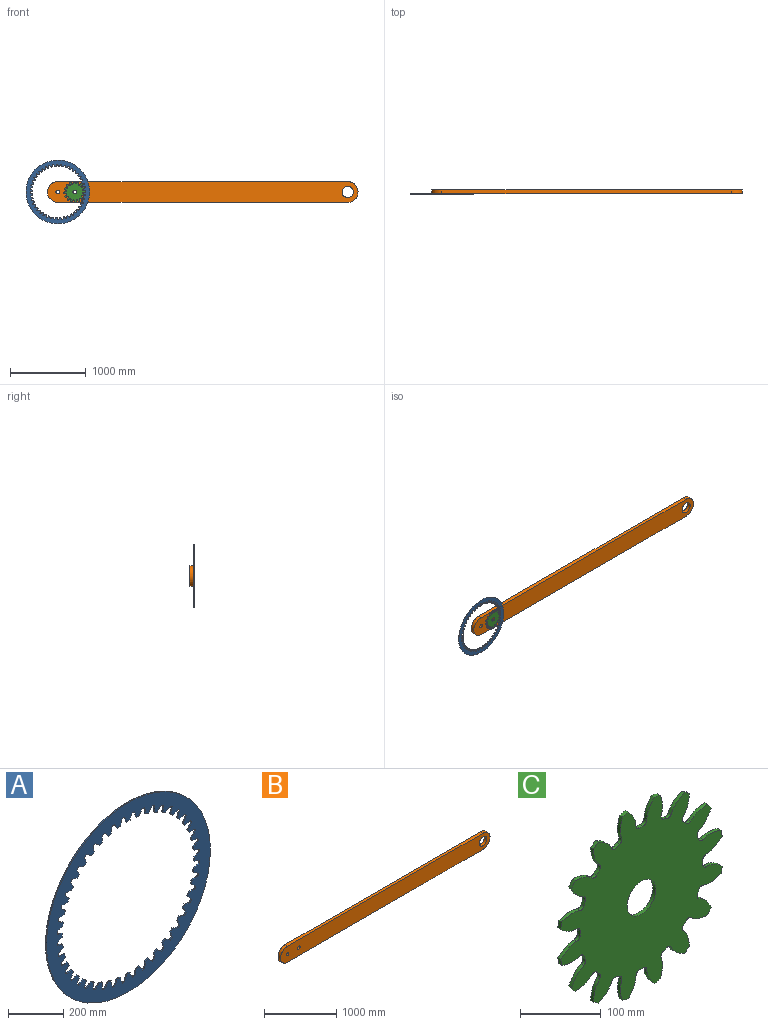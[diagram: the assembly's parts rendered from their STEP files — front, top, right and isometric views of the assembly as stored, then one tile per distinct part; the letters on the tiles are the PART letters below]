
ASSEMBLY  parts=3 mates=2
PART A: 179 faces, bbox 840x5x840 mm
  f0: cylinder r=419.99mm len=839.98mm, axis (0,1,0), area 13194.4mm2, adj f1,f2
  f1: plane 839.98x839.98mm, normal (0,-1,0), area 166526.1mm2, adj f0,f3,f4,f5,f6,f7,f8,f9
  f2: plane 839.98x839.98mm, normal (0,1,0), area 166526.1mm2, adj f0,f3,f4,f5,f6,f7,f8,f9
  f3: cylinder r=365.9mm len=11.89mm, axis (0,1,0), area 60.8mm2, adj f1,f2,f173,f178
  f4: cylinder r=365.9mm len=11.4mm, axis (0,1,0), area 60.8mm2, adj f1,f2,f170,f175
  f5: cylinder r=365.9mm len=10.68mm, axis (0,1,0), area 60.8mm2, adj f1,f2,f167,f172
  f6: cylinder r=365.9mm len=9.74mm, axis (0,1,0), area 60.8mm2, adj f1,f2,f161,f169
  f7: cylinder r=365.9mm len=9.74mm, axis (0,1,0), area 60.8mm2, adj f1,f2,f158,f166
  f8: cylinder r=365.9mm len=8.6mm, axis (0,1,0), area 60.8mm2, adj f1,f2,f163,f164
  f9: cylinder r=365.9mm len=10.68mm, axis (0,1,0), area 60.8mm2, adj f1,f2,f155,f160
  f10: cylinder r=365.9mm len=11.4mm, axis (0,1,0), area 60.8mm2, adj f1,f2,f152,f157
  f11: cylinder r=365.9mm len=11.89mm, axis (0,1,0), area 60.8mm2, adj f1,f2,f149,f154
  f12: cylinder r=365.9mm len=12.14mm, axis (0,1,0), area 60.8mm2, adj f1,f2,f146,f151
  f13: cylinder r=365.9mm len=12.14mm, axis (0,1,0), area 60.8mm2, adj f1,f2,f143,f148
  f14: cylinder r=365.9mm len=11.89mm, axis (0,1,0), area 60.8mm2, adj f1,f2,f140,f145
  f15: cylinder r=365.9mm len=11.4mm, axis (0,1,0), area 60.8mm2, adj f1,f2,f137,f142
  f16: cylinder r=365.9mm len=10.68mm, axis (0,1,0), area 60.8mm2, adj f1,f2,f134,f139
  f17: cylinder r=365.9mm len=9.74mm, axis (0,1,0), area 60.8mm2, adj f1,f2,f131,f136
  f18: cylinder r=365.9mm len=8.6mm, axis (0,1,0), area 60.8mm2, adj f1,f2,f128,f133
  f19: cylinder r=365.9mm len=9.74mm, axis (0,1,0), area 60.8mm2, adj f1,f2,f125,f130
  f20: cylinder r=365.9mm len=10.68mm, axis (0,1,0), area 60.8mm2, adj f1,f2,f122,f127
  f21: cylinder r=365.9mm len=11.4mm, axis (0,1,0), area 60.8mm2, adj f1,f2,f119,f124
  f22: cylinder r=365.9mm len=11.89mm, axis (0,1,0), area 60.8mm2, adj f1,f2,f116,f121
  f23: cylinder r=365.9mm len=12.14mm, axis (0,1,0), area 60.8mm2, adj f1,f2,f113,f118
  f24: cylinder r=365.9mm len=12.14mm, axis (0,1,0), area 60.8mm2, adj f1,f2,f110,f115
  f25: cylinder r=365.9mm len=11.89mm, axis (0,1,0), area 60.8mm2, adj f1,f2,f107,f112
  f26: cylinder r=365.9mm len=11.4mm, axis (0,1,0), area 60.8mm2, adj f1,f2,f104,f109
  f27: cylinder r=365.9mm len=10.68mm, axis (0,1,0), area 60.8mm2, adj f1,f2,f101,f106
  f28: cylinder r=365.9mm len=9.74mm, axis (0,1,0), area 60.8mm2, adj f1,f2,f95,f103
  f29: cylinder r=365.9mm len=9.74mm, axis (0,1,0), area 60.8mm2, adj f1,f2,f92,f100
  f30: cylinder r=365.9mm len=8.6mm, axis (0,1,0), area 60.8mm2, adj f1,f2,f97,f98
  f31: cylinder r=365.9mm len=10.68mm, axis (0,1,0), area 60.8mm2, adj f1,f2,f89,f94
  f32: cylinder r=365.9mm len=11.4mm, axis (0,1,0), area 60.8mm2, adj f1,f2,f86,f91
  f33: cylinder r=365.9mm len=11.89mm, axis (0,1,0), area 60.8mm2, adj f1,f2,f83,f88
  f34: cylinder r=365.9mm len=12.14mm, axis (0,1,0), area 60.8mm2, adj f1,f2,f47,f85
  f35: cylinder r=365.9mm len=12.14mm, axis (0,1,0), area 60.8mm2, adj f1,f2,f82,f176
  f36: cylinder r=365.9mm len=12.14mm, axis (0,1,0), area 60.8mm2, adj f1,f2,f79,f80
  f37: cylinder r=365.9mm len=11.89mm, axis (0,1,0), area 60.8mm2, adj f1,f2,f76,f77
  f38: cylinder r=365.9mm len=11.4mm, axis (0,1,0), area 60.8mm2, adj f1,f2,f73,f74
  f39: cylinder r=365.9mm len=9.74mm, axis (0,1,0), area 60.8mm2, adj f1,f2,f65,f70
  f40: cylinder r=365.9mm len=8.6mm, axis (0,1,0), area 60.8mm2, adj f1,f2,f62,f67
  f41: cylinder r=365.9mm len=9.74mm, axis (0,1,0), area 60.8mm2, adj f1,f2,f59,f64
  f42: cylinder r=365.9mm len=10.68mm, axis (0,1,0), area 60.8mm2, adj f1,f2,f61,f71
  f43: cylinder r=365.9mm len=10.68mm, axis (0,1,0), area 60.8mm2, adj f1,f2,f58,f68
  f44: cylinder r=365.9mm len=11.4mm, axis (0,1,0), area 60.8mm2, adj f1,f2,f55,f56
  f45: cylinder r=365.9mm len=11.89mm, axis (0,1,0), area 60.8mm2, adj f1,f2,f52,f53
  f46: cylinder r=365.9mm len=12.14mm, axis (0,1,0), area 60.8mm2, adj f1,f2,f49,f50
  f47: extruded ~26.87x11.39mm, area 146.3mm2, adj f1,f2,f34,f48
  f48: cylinder r=338.59mm len=17.28mm, axis (0,1,0), area 86.4mm2, adj f1,f2,f47,f49
  f49: extruded ~26.87x11.39mm, area 146.3mm2, adj f1,f2,f46,f48
  f50: extruded ~28.22x7.45mm, area 146.3mm2, adj f1,f2,f46,f51
  f51: cylinder r=338.59mm len=17.1mm, axis (0,1,0), area 86.4mm2, adj f1,f2,f50,f52
  f52: extruded ~24.98x15.1mm, area 146.3mm2, adj f1,f2,f45,f51
  f53: extruded ~28.99x5mm, area 146.3mm2, adj f1,f2,f45,f54
  f54: cylinder r=338.59mm len=16.58mm, axis (0,1,0), area 86.4mm2, adj f1,f2,f53,f55
  f55: extruded ~22.57x18.5mm, area 146.3mm2, adj f1,f2,f44,f54
  f56: extruded ~29.18x5mm, area 146.3mm2, adj f1,f2,f44,f57
  f57: cylinder r=338.59mm len=15.71mm, axis (0,1,0), area 86.4mm2, adj f1,f2,f56,f58
  f58: extruded ~21.53x19.71mm, area 146.3mm2, adj f1,f2,f43,f57
  f59: extruded ~24.11x16.45mm, area 146.3mm2, adj f1,f2,f41,f60
  f60: cylinder r=338.59mm len=14.53mm, axis (0,1,0), area 86.4mm2, adj f1,f2,f59,f61
  f61: extruded ~28.77x5mm, area 146.3mm2, adj f1,f2,f42,f60
  f62: extruded ~26.21x12.85mm, area 146.3mm2, adj f1,f2,f40,f63
  f63: cylinder r=338.59mm len=13.06mm, axis (0,1,0), area 86.4mm2, adj f1,f2,f62,f64
  f64: extruded ~27.77x8.99mm, area 146.3mm2, adj f1,f2,f41,f63
  f65: extruded ~27.77x8.99mm, area 146.3mm2, adj f1,f2,f39,f66
  f66: cylinder r=338.59mm len=13.06mm, axis (0,1,0), area 86.4mm2, adj f1,f2,f65,f67
  f67: extruded ~26.21x12.85mm, area 146.3mm2, adj f1,f2,f40,f66
  f68: extruded ~28.77x5mm, area 146.3mm2, adj f1,f2,f43,f69
  f69: cylinder r=338.59mm len=14.53mm, axis (0,1,0), area 86.4mm2, adj f1,f2,f68,f70
  f70: extruded ~24.11x16.45mm, area 146.3mm2, adj f1,f2,f39,f69
  f71: extruded ~21.53x19.71mm, area 146.3mm2, adj f1,f2,f42,f72
  f72: cylinder r=338.59mm len=15.71mm, axis (0,1,0), area 86.4mm2, adj f1,f2,f71,f73
  f73: extruded ~29.18x5mm, area 146.3mm2, adj f1,f2,f38,f72
  f74: extruded ~22.57x18.5mm, area 146.3mm2, adj f1,f2,f38,f75
  f75: cylinder r=338.59mm len=16.58mm, axis (0,1,0), area 86.4mm2, adj f1,f2,f74,f76
  f76: extruded ~28.99x5mm, area 146.3mm2, adj f1,f2,f37,f75
  f77: extruded ~24.98x15.1mm, area 146.3mm2, adj f1,f2,f37,f78
  f78: cylinder r=338.59mm len=17.1mm, axis (0,1,0), area 86.4mm2, adj f1,f2,f77,f79
  f79: extruded ~28.22x7.45mm, area 146.3mm2, adj f1,f2,f36,f78
  f80: extruded ~26.87x11.39mm, area 146.3mm2, adj f1,f2,f36,f81
  f81: cylinder r=338.59mm len=17.28mm, axis (0,1,0), area 86.4mm2, adj f1,f2,f80,f82
  f82: extruded ~26.87x11.39mm, area 146.3mm2, adj f1,f2,f35,f81
  f83: extruded ~24.98x15.1mm, area 146.3mm2, adj f1,f2,f33,f84
  f84: cylinder r=338.59mm len=17.1mm, axis (0,1,0), area 86.4mm2, adj f1,f2,f83,f85
  f85: extruded ~28.22x7.45mm, area 146.3mm2, adj f1,f2,f34,f84
  f86: extruded ~22.57x18.5mm, area 146.3mm2, adj f1,f2,f32,f87
  f87: cylinder r=338.59mm len=16.58mm, axis (0,1,0), area 86.4mm2, adj f1,f2,f86,f88
  f88: extruded ~28.99x5mm, area 146.3mm2, adj f1,f2,f33,f87
  f89: extruded ~21.53x19.71mm, area 146.3mm2, adj f1,f2,f31,f90
  f90: cylinder r=338.59mm len=15.71mm, axis (0,1,0), area 86.4mm2, adj f1,f2,f89,f91
  f91: extruded ~29.18x5mm, area 146.3mm2, adj f1,f2,f32,f90
  f92: extruded ~24.11x16.45mm, area 146.3mm2, adj f1,f2,f29,f93
  f93: cylinder r=338.59mm len=14.53mm, axis (0,1,0), area 86.4mm2, adj f1,f2,f92,f94
  f94: extruded ~28.77x5mm, area 146.3mm2, adj f1,f2,f31,f93
  f95: extruded ~27.77x8.99mm, area 146.3mm2, adj f1,f2,f28,f96
  f96: cylinder r=338.59mm len=13.06mm, axis (0,1,0), area 86.4mm2, adj f1,f2,f95,f97
  f97: extruded ~26.21x12.85mm, area 146.3mm2, adj f1,f2,f30,f96
  f98: extruded ~26.21x12.85mm, area 146.3mm2, adj f1,f2,f30,f99
  f99: cylinder r=338.59mm len=13.06mm, axis (0,1,0), area 86.4mm2, adj f1,f2,f98,f100
  f100: extruded ~27.77x8.99mm, area 146.3mm2, adj f1,f2,f29,f99
  f101: extruded ~28.77x5mm, area 146.3mm2, adj f1,f2,f27,f102
  f102: cylinder r=338.59mm len=14.53mm, axis (0,1,0), area 86.4mm2, adj f1,f2,f101,f103
  f103: extruded ~24.11x16.45mm, area 146.3mm2, adj f1,f2,f28,f102
  f104: extruded ~29.18x5mm, area 146.3mm2, adj f1,f2,f26,f105
  f105: cylinder r=338.59mm len=15.71mm, axis (0,1,0), area 86.4mm2, adj f1,f2,f104,f106
  f106: extruded ~21.53x19.71mm, area 146.3mm2, adj f1,f2,f27,f105
  f107: extruded ~28.99x5mm, area 146.3mm2, adj f1,f2,f25,f108
  f108: cylinder r=338.59mm len=16.58mm, axis (0,1,0), area 86.4mm2, adj f1,f2,f107,f109
  f109: extruded ~22.57x18.5mm, area 146.3mm2, adj f1,f2,f26,f108
  f110: extruded ~28.22x7.45mm, area 146.3mm2, adj f1,f2,f24,f111
  f111: cylinder r=338.59mm len=17.1mm, axis (0,1,0), area 86.4mm2, adj f1,f2,f110,f112
  f112: extruded ~24.98x15.1mm, area 146.3mm2, adj f1,f2,f25,f111
  f113: extruded ~26.87x11.39mm, area 146.3mm2, adj f1,f2,f23,f114
  f114: cylinder r=338.59mm len=17.28mm, axis (0,1,0), area 86.4mm2, adj f1,f2,f113,f115
  f115: extruded ~26.87x11.39mm, area 146.3mm2, adj f1,f2,f24,f114
  f116: extruded ~24.98x15.1mm, area 146.3mm2, adj f1,f2,f22,f117
  f117: cylinder r=338.59mm len=17.1mm, axis (0,1,0), area 86.4mm2, adj f1,f2,f116,f118
  f118: extruded ~28.22x7.45mm, area 146.3mm2, adj f1,f2,f23,f117
  f119: extruded ~22.57x18.5mm, area 146.3mm2, adj f1,f2,f21,f120
  f120: cylinder r=338.59mm len=16.58mm, axis (0,1,0), area 86.4mm2, adj f1,f2,f119,f121
  f121: extruded ~28.99x5mm, area 146.3mm2, adj f1,f2,f22,f120
  f122: extruded ~21.53x19.71mm, area 146.3mm2, adj f1,f2,f20,f123
  f123: cylinder r=338.59mm len=15.71mm, axis (0,1,0), area 86.4mm2, adj f1,f2,f122,f124
  f124: extruded ~29.18x5mm, area 146.3mm2, adj f1,f2,f21,f123
  f125: extruded ~24.11x16.45mm, area 146.3mm2, adj f1,f2,f19,f126
  f126: cylinder r=338.59mm len=14.53mm, axis (0,1,0), area 86.4mm2, adj f1,f2,f125,f127
  f127: extruded ~28.77x5mm, area 146.3mm2, adj f1,f2,f20,f126
  f128: extruded ~26.21x12.85mm, area 146.3mm2, adj f1,f2,f18,f129
  f129: cylinder r=338.59mm len=13.06mm, axis (0,1,0), area 86.4mm2, adj f1,f2,f128,f130
  f130: extruded ~27.77x8.99mm, area 146.3mm2, adj f1,f2,f19,f129
  f131: extruded ~27.77x8.99mm, area 146.3mm2, adj f1,f2,f17,f132
  f132: cylinder r=338.59mm len=13.06mm, axis (0,1,0), area 86.4mm2, adj f1,f2,f131,f133
  f133: extruded ~26.21x12.85mm, area 146.3mm2, adj f1,f2,f18,f132
  f134: extruded ~28.77x5mm, area 146.3mm2, adj f1,f2,f16,f135
  f135: cylinder r=338.59mm len=14.53mm, axis (0,1,0), area 86.4mm2, adj f1,f2,f134,f136
  f136: extruded ~24.11x16.45mm, area 146.3mm2, adj f1,f2,f17,f135
  f137: extruded ~29.18x5mm, area 146.3mm2, adj f1,f2,f15,f138
  f138: cylinder r=338.59mm len=15.71mm, axis (0,1,0), area 86.4mm2, adj f1,f2,f137,f139
  f139: extruded ~21.53x19.71mm, area 146.3mm2, adj f1,f2,f16,f138
  f140: extruded ~28.99x5mm, area 146.3mm2, adj f1,f2,f14,f141
  f141: cylinder r=338.59mm len=16.58mm, axis (0,1,0), area 86.4mm2, adj f1,f2,f140,f142
  f142: extruded ~22.57x18.5mm, area 146.3mm2, adj f1,f2,f15,f141
  f143: extruded ~28.22x7.45mm, area 146.3mm2, adj f1,f2,f13,f144
  f144: cylinder r=338.59mm len=17.1mm, axis (0,1,0), area 86.4mm2, adj f1,f2,f143,f145
  f145: extruded ~24.98x15.1mm, area 146.3mm2, adj f1,f2,f14,f144
  f146: extruded ~26.87x11.39mm, area 146.3mm2, adj f1,f2,f12,f147
  f147: cylinder r=338.59mm len=17.28mm, axis (0,1,0), area 86.4mm2, adj f1,f2,f146,f148
  f148: extruded ~26.87x11.39mm, area 146.3mm2, adj f1,f2,f13,f147
  f149: extruded ~24.98x15.1mm, area 146.3mm2, adj f1,f2,f11,f150
  f150: cylinder r=338.59mm len=17.1mm, axis (0,1,0), area 86.4mm2, adj f1,f2,f149,f151
  f151: extruded ~28.22x7.45mm, area 146.3mm2, adj f1,f2,f12,f150
  f152: extruded ~22.57x18.5mm, area 146.3mm2, adj f1,f2,f10,f153
  f153: cylinder r=338.59mm len=16.58mm, axis (0,1,0), area 86.4mm2, adj f1,f2,f152,f154
  f154: extruded ~28.99x5mm, area 146.3mm2, adj f1,f2,f11,f153
  f155: extruded ~21.53x19.71mm, area 146.3mm2, adj f1,f2,f9,f156
  f156: cylinder r=338.59mm len=15.71mm, axis (0,1,0), area 86.4mm2, adj f1,f2,f155,f157
  f157: extruded ~29.18x5mm, area 146.3mm2, adj f1,f2,f10,f156
  f158: extruded ~24.11x16.45mm, area 146.3mm2, adj f1,f2,f7,f159
  f159: cylinder r=338.59mm len=14.53mm, axis (0,1,0), area 86.4mm2, adj f1,f2,f158,f160
  f160: extruded ~28.77x5mm, area 146.3mm2, adj f1,f2,f9,f159
  f161: extruded ~27.77x8.99mm, area 146.3mm2, adj f1,f2,f6,f162
  f162: cylinder r=338.59mm len=13.06mm, axis (0,1,0), area 86.4mm2, adj f1,f2,f161,f163
  f163: extruded ~26.21x12.85mm, area 146.3mm2, adj f1,f2,f8,f162
  f164: extruded ~26.21x12.85mm, area 146.3mm2, adj f1,f2,f8,f165
  f165: cylinder r=338.59mm len=13.06mm, axis (0,1,0), area 86.4mm2, adj f1,f2,f164,f166
  f166: extruded ~27.77x8.99mm, area 146.3mm2, adj f1,f2,f7,f165
  f167: extruded ~28.77x5mm, area 146.3mm2, adj f1,f2,f5,f168
  f168: cylinder r=338.59mm len=14.53mm, axis (0,1,0), area 86.4mm2, adj f1,f2,f167,f169
  f169: extruded ~24.11x16.45mm, area 146.3mm2, adj f1,f2,f6,f168
  f170: extruded ~29.18x5mm, area 146.3mm2, adj f1,f2,f4,f171
  f171: cylinder r=338.59mm len=15.71mm, axis (0,1,0), area 86.4mm2, adj f1,f2,f170,f172
  f172: extruded ~21.53x19.71mm, area 146.3mm2, adj f1,f2,f5,f171
  f173: extruded ~28.99x5mm, area 146.3mm2, adj f1,f2,f3,f174
  f174: cylinder r=338.59mm len=16.58mm, axis (0,1,0), area 86.4mm2, adj f1,f2,f173,f175
  f175: extruded ~22.57x18.5mm, area 146.3mm2, adj f1,f2,f4,f174
  f176: extruded ~28.22x7.45mm, area 146.3mm2, adj f1,f2,f35,f177
  f177: cylinder r=338.59mm len=17.1mm, axis (0,1,0), area 86.4mm2, adj f1,f2,f176,f178
  f178: extruded ~24.98x15.1mm, area 146.3mm2, adj f1,f2,f3,f177
PART B: 9 faces, bbox 4181.6x50x272 mm
  f0: plane 3828x50mm, normal (0,0,-1), area 191400mm2, adj f1,f6,f7,f8
  f1: extruded ~272x136mm, area 21362.8mm2, adj f0,f2,f7,f8
  f2: plane 3828x50mm, normal (0,0,1), area 191400mm2, adj f1,f6,f7,f8
  f3: cylinder r=75mm len=150mm, axis (0,1,0), area 23561.9mm2, adj f7,f8
  f4: cylinder r=25mm len=50mm, axis (0,1,0), area 7854mm2, adj f7,f8
  f5: cylinder r=25mm len=50mm, axis (0,1,0), area 7854mm2, adj f7,f8
  f6: extruded ~272x136mm, area 21362.8mm2, adj f0,f2,f7,f8
  f7: plane 4181.6x272mm, normal (0,-1,0), area 1077690.6mm2, adj f0,f1,f2,f3,f4,f5,f6
  f8: plane 4181.6x272mm, normal (0,1,0), area 1077690.6mm2, adj f0,f1,f2,f3,f4,f5,f6
PART C: 99 faces, bbox 283.1x5x283.1 mm
  f0: extruded ~28.56x13.33mm, area 161.7mm2, adj f64,f65,f66,f67
  f1: cylinder r=107.37mm len=6.56mm, axis (0,1,0), area 32.8mm2, adj f65,f66,f67,f68
  f2: extruded ~28.56x13.33mm, area 161.7mm2, adj f3,f65,f66,f68
  f3: cylinder r=143.16mm len=10.38mm, axis (0,1,0), area 52.9mm2, adj f2,f4,f65,f66
  f4: extruded ~31.48x5mm, area 161.7mm2, adj f3,f65,f66,f69
  f5: cylinder r=107.37mm len=6.06mm, axis (0,1,0), area 32.8mm2, adj f65,f66,f69,f70
  f6: extruded ~23.24x21.28mm, area 161.7mm2, adj f7,f65,f66,f70
  f7: cylinder r=143.16mm len=8.8mm, axis (0,1,0), area 52.9mm2, adj f6,f8,f65,f66
  f8: extruded ~29.62x10.77mm, area 161.7mm2, adj f7,f65,f66,f71
  f9: cylinder r=107.37mm len=5mm, axis (0,1,0), area 32.8mm2, adj f65,f66,f71,f72
  f10: extruded ~29.62x10.77mm, area 161.7mm2, adj f11,f65,f66,f72
  f11: cylinder r=143.16mm len=8.8mm, axis (0,1,0), area 52.9mm2, adj f10,f12,f65,f66
  f12: extruded ~23.24x21.28mm, area 161.7mm2, adj f11,f65,f66,f73
  f13: cylinder r=107.37mm len=6.06mm, axis (0,1,0), area 32.8mm2, adj f65,f66,f73,f74
  f14: extruded ~31.48x5mm, area 161.7mm2, adj f15,f65,f66,f74
  f15: cylinder r=143.16mm len=10.38mm, axis (0,1,0), area 52.9mm2, adj f14,f16,f65,f66
  f16: extruded ~28.56x13.33mm, area 161.7mm2, adj f15,f65,f66,f75
  f17: cylinder r=107.37mm len=6.56mm, axis (0,1,0), area 32.8mm2, adj f65,f66,f75,f76
  f18: extruded ~28.56x13.33mm, area 161.7mm2, adj f19,f65,f66,f76
  f19: cylinder r=143.16mm len=10.38mm, axis (0,1,0), area 52.9mm2, adj f18,f20,f65,f66
  f20: extruded ~31.48x5mm, area 161.7mm2, adj f19,f65,f66,f77
  f21: cylinder r=107.37mm len=6.06mm, axis (0,1,0), area 32.8mm2, adj f65,f66,f77,f78
  f22: extruded ~23.24x21.28mm, area 161.7mm2, adj f23,f65,f66,f78
  f23: cylinder r=143.16mm len=8.8mm, axis (0,1,0), area 52.9mm2, adj f22,f24,f65,f66
  f24: extruded ~29.62x10.77mm, area 161.7mm2, adj f23,f65,f66,f79
  f25: cylinder r=107.37mm len=5mm, axis (0,1,0), area 32.8mm2, adj f65,f66,f79,f80
  f26: extruded ~29.62x10.77mm, area 161.7mm2, adj f27,f65,f66,f80
  f27: cylinder r=143.16mm len=8.8mm, axis (0,1,0), area 52.9mm2, adj f26,f28,f65,f66
  f28: extruded ~23.24x21.28mm, area 161.7mm2, adj f27,f65,f66,f81
  f29: cylinder r=107.37mm len=6.06mm, axis (0,1,0), area 32.8mm2, adj f65,f66,f81,f82
  f30: extruded ~31.48x5mm, area 161.7mm2, adj f31,f65,f66,f82
  f31: cylinder r=143.16mm len=10.38mm, axis (0,1,0), area 52.9mm2, adj f30,f32,f65,f66
  f32: extruded ~28.56x13.33mm, area 161.7mm2, adj f31,f65,f66,f83
  f33: cylinder r=107.37mm len=6.56mm, axis (0,1,0), area 32.8mm2, adj f65,f66,f83,f84
  f34: extruded ~28.56x13.33mm, area 161.7mm2, adj f35,f65,f66,f84
  f35: cylinder r=143.16mm len=10.38mm, axis (0,1,0), area 52.9mm2, adj f34,f36,f65,f66
  f36: extruded ~31.48x5mm, area 161.7mm2, adj f35,f65,f66,f85
  f37: cylinder r=107.37mm len=6.06mm, axis (0,1,0), area 32.8mm2, adj f65,f66,f85,f86
  f38: extruded ~23.24x21.28mm, area 161.7mm2, adj f39,f65,f66,f86
  f39: cylinder r=143.16mm len=8.8mm, axis (0,1,0), area 52.9mm2, adj f38,f40,f65,f66
  f40: extruded ~29.62x10.77mm, area 161.7mm2, adj f39,f65,f66,f87
  f41: cylinder r=107.37mm len=5mm, axis (0,1,0), area 32.8mm2, adj f65,f66,f87,f88
  f42: extruded ~29.62x10.77mm, area 161.7mm2, adj f43,f65,f66,f88
  f43: cylinder r=143.16mm len=8.8mm, axis (0,1,0), area 52.9mm2, adj f42,f44,f65,f66
  f44: extruded ~23.24x21.28mm, area 161.7mm2, adj f43,f65,f66,f89
  f45: cylinder r=107.37mm len=6.06mm, axis (0,1,0), area 32.8mm2, adj f65,f66,f89,f90
  f46: extruded ~31.48x5mm, area 161.7mm2, adj f47,f65,f66,f90
  f47: cylinder r=143.16mm len=10.38mm, axis (0,1,0), area 52.9mm2, adj f46,f48,f65,f66
  f48: extruded ~28.56x13.33mm, area 161.7mm2, adj f47,f65,f66,f91
  f49: cylinder r=107.37mm len=6.56mm, axis (0,1,0), area 32.8mm2, adj f65,f66,f91,f92
  f50: extruded ~28.56x13.33mm, area 161.7mm2, adj f51,f65,f66,f92
  f51: cylinder r=143.16mm len=10.38mm, axis (0,1,0), area 52.9mm2, adj f50,f52,f65,f66
  f52: extruded ~31.48x5mm, area 161.7mm2, adj f51,f65,f66,f93
  f53: cylinder r=107.37mm len=6.06mm, axis (0,1,0), area 32.8mm2, adj f65,f66,f93,f94
  f54: extruded ~23.24x21.28mm, area 161.7mm2, adj f55,f65,f66,f94
  f55: cylinder r=143.16mm len=8.8mm, axis (0,1,0), area 52.9mm2, adj f54,f56,f65,f66
  f56: extruded ~29.62x10.77mm, area 161.7mm2, adj f55,f65,f66,f95
  f57: cylinder r=107.37mm len=5mm, axis (0,1,0), area 32.8mm2, adj f65,f66,f95,f96
  f58: extruded ~29.62x10.77mm, area 161.7mm2, adj f59,f65,f66,f96
  f59: cylinder r=143.16mm len=8.8mm, axis (0,1,0), area 52.9mm2, adj f58,f60,f65,f66
  f60: extruded ~23.24x21.28mm, area 161.7mm2, adj f59,f65,f66,f97
  f61: cylinder r=107.37mm len=6.06mm, axis (0,1,0), area 32.8mm2, adj f65,f66,f97,f98
  f62: extruded ~31.48x5mm, area 161.7mm2, adj f64,f65,f66,f98
  f63: cylinder r=25mm len=50mm, axis (0,1,0), area 785.4mm2, adj f65,f66
  f64: cylinder r=143.16mm len=10.38mm, axis (0,1,0), area 52.9mm2, adj f0,f62,f65,f66
  f65: plane 283.08x283.08mm, normal (0,-1,0), area 47502.4mm2, adj f0,f1,f2,f3,f4,f5,f6,f7
  f66: plane 283.08x283.08mm, normal (0,1,0), area 47502.4mm2, adj f0,f1,f2,f3,f4,f5,f6,f7
  f67: cylinder r=5.95mm len=6.12mm, axis (0,1,0), area 45.3mm2, adj f0,f1,f65,f66
  f68: cylinder r=5.95mm len=6.12mm, axis (0,1,0), area 45.3mm2, adj f1,f2,f65,f66
  f69: cylinder r=5.95mm len=7.39mm, axis (0,1,0), area 45.3mm2, adj f4,f5,f65,f66
  f70: cylinder r=5.95mm len=7.74mm, axis (0,1,0), area 45.3mm2, adj f5,f6,f65,f66
  f71: cylinder r=5.95mm len=8.19mm, axis (0,1,0), area 45.3mm2, adj f8,f9,f65,f66
  f72: cylinder r=5.95mm len=8.19mm, axis (0,1,0), area 45.3mm2, adj f9,f10,f65,f66
  f73: cylinder r=5.95mm len=7.74mm, axis (0,1,0), area 45.3mm2, adj f12,f13,f65,f66
  f74: cylinder r=5.95mm len=7.39mm, axis (0,1,0), area 45.3mm2, adj f13,f14,f65,f66
  f75: cylinder r=5.95mm len=6.12mm, axis (0,1,0), area 45.3mm2, adj f16,f17,f65,f66
  f76: cylinder r=5.95mm len=6.12mm, axis (0,1,0), area 45.3mm2, adj f17,f18,f65,f66
  f77: cylinder r=5.95mm len=7.39mm, axis (0,1,0), area 45.3mm2, adj f20,f21,f65,f66
  f78: cylinder r=5.95mm len=7.74mm, axis (0,1,0), area 45.3mm2, adj f21,f22,f65,f66
  f79: cylinder r=5.95mm len=8.19mm, axis (0,1,0), area 45.3mm2, adj f24,f25,f65,f66
  f80: cylinder r=5.95mm len=8.19mm, axis (0,1,0), area 45.3mm2, adj f25,f26,f65,f66
  f81: cylinder r=5.95mm len=7.74mm, axis (0,1,0), area 45.3mm2, adj f28,f29,f65,f66
  f82: cylinder r=5.95mm len=7.39mm, axis (0,1,0), area 45.3mm2, adj f29,f30,f65,f66
  f83: cylinder r=5.95mm len=6.12mm, axis (0,1,0), area 45.3mm2, adj f32,f33,f65,f66
  f84: cylinder r=5.95mm len=6.12mm, axis (0,1,0), area 45.3mm2, adj f33,f34,f65,f66
  f85: cylinder r=5.95mm len=7.39mm, axis (0,1,0), area 45.3mm2, adj f36,f37,f65,f66
  f86: cylinder r=5.95mm len=7.74mm, axis (0,1,0), area 45.3mm2, adj f37,f38,f65,f66
  f87: cylinder r=5.95mm len=8.19mm, axis (0,1,0), area 45.3mm2, adj f40,f41,f65,f66
  f88: cylinder r=5.95mm len=8.19mm, axis (0,1,0), area 45.3mm2, adj f41,f42,f65,f66
  f89: cylinder r=5.95mm len=7.74mm, axis (0,1,0), area 45.3mm2, adj f44,f45,f65,f66
  f90: cylinder r=5.95mm len=7.39mm, axis (0,1,0), area 45.3mm2, adj f45,f46,f65,f66
  f91: cylinder r=5.95mm len=6.12mm, axis (0,1,0), area 45.3mm2, adj f48,f49,f65,f66
  f92: cylinder r=5.95mm len=6.12mm, axis (0,1,0), area 45.3mm2, adj f49,f50,f65,f66
  f93: cylinder r=5.95mm len=7.39mm, axis (0,1,0), area 45.3mm2, adj f52,f53,f65,f66
  f94: cylinder r=5.95mm len=7.74mm, axis (0,1,0), area 45.3mm2, adj f53,f54,f65,f66
  f95: cylinder r=5.95mm len=8.19mm, axis (0,1,0), area 45.3mm2, adj f56,f57,f65,f66
  f96: cylinder r=5.95mm len=8.19mm, axis (0,1,0), area 45.3mm2, adj f57,f58,f65,f66
  f97: cylinder r=5.95mm len=7.74mm, axis (0,1,0), area 45.3mm2, adj f60,f61,f65,f66
  f98: cylinder r=5.95mm len=7.39mm, axis (0,1,0), area 45.3mm2, adj f61,f62,f65,f66
PLACE A rot(axis=(0,-1,0),136.3deg) t=(-294.19,-3.16,776.25)mm
PLACE B t=(3533.81,46.84,640.25)mm fixed
PLACE C rot(axis=(0,-1,0),104.8deg) t=(-71.51,-3.16,776.25)mm
MATE revolute A.f0 <-> B.f4  axis (0,1,0) through (-294.19,-3.16,776.25)mm
MATE revolute C.f3 <-> B.f5  axis (0,1,0) through (-71.51,-3.16,776.25)mm
